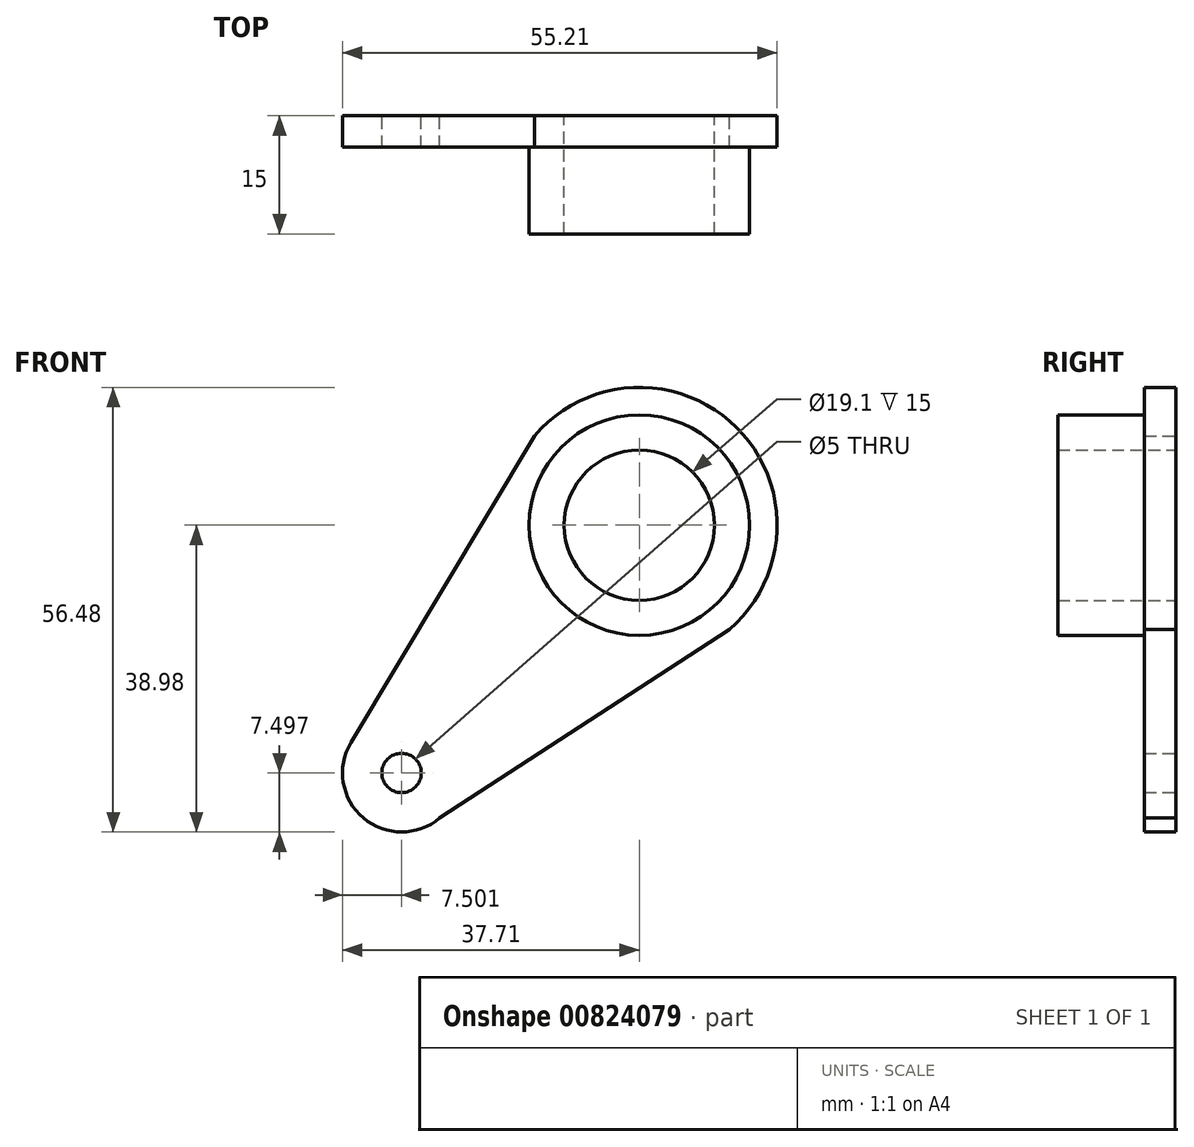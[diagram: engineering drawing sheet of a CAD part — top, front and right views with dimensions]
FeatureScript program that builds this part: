
annotation { "Feature Type Name" : "Feature", "Feature Type Description" : "" }
export const myFeature = defineFeature(function(context is Context, id is Id, definition is map)
    precondition{}
    {
        {
            var Q0;
            Q0=qCreatedBy(makeId("Front.planeOp"),FACE);
            var sketch = newSketch(context, id + "F0", { "sketchPlane" : qUnion([Q0])});
            skCircle(sketch, "E0", {"center": v(0, 0) * mm, "radius": 14 * mm});
            skCircle(sketch, "E1", {"center": v(-30.2, -31.48) * mm, "radius": 2.5 * mm});
            skLineSegment(sketch, "E2", {"start": v(-25.37, -37.21) * mm, "end": v(-25.37, -37.21) * mm});
            skLineSegment(sketch, "E3", {"start": v(-13.32, 11.35) * mm, "end": v(-36.65, -27.63) * mm});
            skLineSegment(sketch, "E4", {"start": v(11.43, -13.26) * mm, "end": v(11.43, -13.26) * mm});
            skArc(sketch, "E5", {"start": v(11.43, -13.26) * mm, "mid": v(12.34, 12.4) * mm, "end": v(-13.32, 11.35) * mm});
            skLineSegment(sketch, "E6", {"start": v(-40.11, -25.63) * mm, "end": v(-40.11, -25.63) * mm});
            skLineSegment(sketch, "E7", {"start": v(-25.37, -37.21) * mm, "end": v(11.43, -13.26) * mm});
            skArc(sketch, "E8", {"start": v(-36.65, -27.63) * mm, "mid": v(-35.06, -37.2) * mm, "end": v(-25.37, -37.21) * mm});
            skCircle(sketch, "E9", {"center": v(0, 0) * mm, "radius": 9.55 * mm});
            skSolve(sketch);
        }
        {
            var Q0;
            Q0=makeQuery(id+"F0.imprint","IMPRINT",FACE,{"disambiguationData":[TD([[makeQuery(id+"F0.imprint","IMPRINT",EDGE,{"derivedFrom":sQuery(id+"F0.wireOp",EDGE,"E0")}),1.0]])]});
            extrude(context, id + "F1", {"entities" : qUnion([Q0]), "depth" : 15 * mm, "offsetDistance" : 25 * mm});
        }
        {
            var Q0;
            Q0=makeQuery(id+"F0.imprint","IMPRINT",FACE,{"disambiguationData":[TD([[makeQuery(id+"F0.imprint","IMPRINT",EDGE,{"derivedFrom":sQuery(id+"F0.wireOp",EDGE,"E0")}),-1.0]])]});
            var Q1;
            Q1=sQuery(id+"F0.wireOp",EDGE,"C4IzJziD-EfBM-hj3k-gTeQ-GYtw3utJK5uY");
            var Q2;
            Q2=sQuery(id+"F0.wireOp",EDGE,"2fb015ca-b637-436b-9bb4-65c2bbf925fc1");
            var Q3;
            Q3=sQuery(id+"F0.wireOp",EDGE,"E5");
            var Q4;
            Q4=sQuery(id+"F0.wireOp",EDGE,"E3");
            var Q5;
            Q5=sQuery(id+"F0.wireOp",EDGE,"E7");
            var Q6;
            Q6=sQuery(id+"F0.wireOp",EDGE,"vvoXQS7o-CLwH-2vEG-14Dp-gcNSuJNAZMJY");
            var Q7;
            Q7=sQuery(id+"F0.wireOp",EDGE,"5a462c73-721c-4efd-93b1-083839a0a5502");
            var Q8;
            Q8=sQuery(id+"F0.wireOp",EDGE,"E8");
            extrude(context, id + "F2", {"entities" : qUnion([Q0]), "operationType" : NewBodyOperationType.ADD, "surfaceEntities" : qUnion([Q1, Q2, Q3, Q4, Q5, Q6, Q7, Q8]), "depth" : 4 * mm, "offsetDistance" : 25 * mm});
        }
    });
